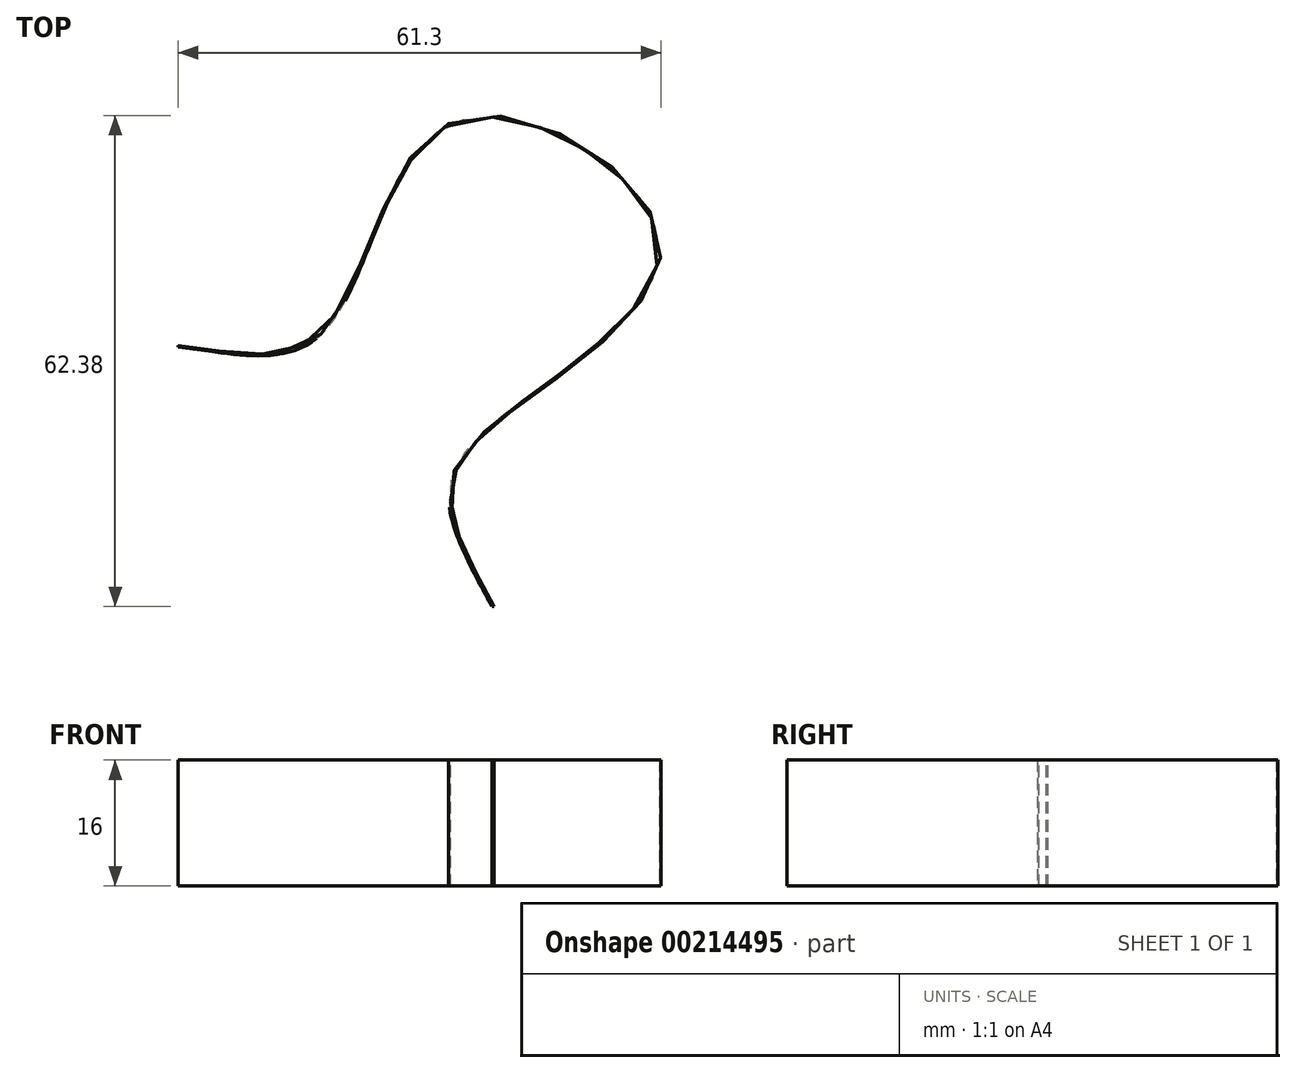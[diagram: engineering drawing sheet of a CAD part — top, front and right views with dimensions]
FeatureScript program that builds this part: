
annotation { "Feature Type Name" : "Feature", "Feature Type Description" : "" }
export const myFeature = defineFeature(function(context is Context, id is Id, definition is map)
    precondition{}
    {
        {
            var Q0;
            Q0=qCreatedBy(makeId("Top.planeOp"),FACE);
            var sketch = newSketch(context, id + "F0", { "sketchPlane" : qUnion([Q0])});
            skLineSegment(sketch, "E0.bottom", {"start": v(-49.02, 68.55) * mm, "end": v(50.98, 68.55) * mm});
            skLineSegment(sketch, "E0.top", {"start": v(-49.02, -1.45) * mm, "end": v(50.98, -1.45) * mm});
            skLineSegment(sketch, "E0.left", {"start": v(-49.02, 68.55) * mm, "end": v(-49.02, -1.45) * mm});
            skLineSegment(sketch, "E0.right", {"start": v(50.98, 68.55) * mm, "end": v(50.98, -1.45) * mm});
            skSolve(sketch);
        }
        {
            var Q0;
            Q0=makeQuery(id+"F0.imprint","IMPRINT",FACE,{"disambiguationData":[TD([[makeQuery(id+"F0.imprint","IMPRINT",EDGE,{"derivedFrom":sQuery(id+"F0.wireOp",EDGE,"E0.bottom")}),-1.0]])]});
            extrude(context, id + "F1", {"entities" : qUnion([Q0]), "depth" : 16 * mm});
        }
        {
            var Q0;
            Q0=makeQuery(id+"F1.opExtrude","CAP_FACE",FACE,{"disambiguationData":[OSD([sQuery(id+"F0.wireOp",EDGE,"E0.bottom"),sQuery(id+"F0.wireOp",EDGE,"E0.top"),sQuery(id+"F0.wireOp",EDGE,"E0.left"),sQuery(id+"F0.wireOp",EDGE,"E0.right")])],"isStart":false});
            var sketch = newSketch(context, id + "F2", { "sketchPlane" : qUnion([Q0])});
            skFitSpline(sketch, "E1", {"points": [v(-49.02, 32.72) * mm, v(-31.2, 34.1) * mm, v(-14.12, 61.19) * mm, v(12.2, 46.15) * mm, v(-7.24, 23.93) * mm, v(-14.44, 12.73) * mm, v(-8.38, -1.45) * mm], "startDerivative": vector(112.66, -9.86) * mm, "endDerivative": vector(43.43, -83.27) * mm});
            skSolve(sketch);
        }
        {
            var Q0;
            {var subQ5=makeQuery(id+"F1.opExtrude","CAP_EDGE",EDGE,{"disambiguationData":[OSD([sQuery(id+"F0.wireOp",EDGE,"E0.right")])],"isStart":false});Q0=makeQuery(id+"F2.imprint","IMPRINT",FACE,{"disambiguationData":[TD([[makeQuery(id+"F2.imprint","IMPRINT",EDGE,{"derivedFrom":subQ5}),-1.0]])]});}
            var Q1;
            {var subQ0=sQuery(id+"F2.wireOp",EDGE,"f820d5b4-2767-42e3-97d1-27e4c2d8213b");var subQ1=makeQuery(id+"F1.opExtrude","CAP_EDGE",EDGE,{"disambiguationData":[OSD([sQuery(id+"F0.wireOp",EDGE,"E0.left")])],"isStart":false});var subQ2=makeQuery(id+"F2.imprint","INTERSECT",VERTEX,{"derivedFrom":[subQ1,subQ0]});Q1=makeQuery(id+"F2.imprint","IMPRINT",FACE,{"disambiguationData":[TD([[makeQuery(id+"F2.imprint","IMPRINT",EDGE,{"disambiguationData":[TD([[subQ2,-1.0]])],"derivedFrom":subQ0}),1.0]])]});}
            extrude(context, id + "F3", {"entities" : qUnion([Q0, Q1]), "operationType" : NewBodyOperationType.REMOVE, "oppositeDirection" : true, "depth" : 25 * mm});
        }
        {
            var Q0;
            Q0=makeQuery(id+"F1.opExtrude","CAP_FACE",FACE,{"disambiguationData":[OSD([sQuery(id+"F0.wireOp",EDGE,"E0.bottom"),sQuery(id+"F0.wireOp",EDGE,"E0.top"),sQuery(id+"F0.wireOp",EDGE,"E0.left"),sQuery(id+"F0.wireOp",EDGE,"E0.right")])],"isStart":false});
            var Q1;
            Q1=makeQuery(id+"F1.opExtrude","CAP_FACE",FACE,{"disambiguationData":[OSD([sQuery(id+"F0.wireOp",EDGE,"E0.bottom"),sQuery(id+"F0.wireOp",EDGE,"E0.top"),sQuery(id+"F0.wireOp",EDGE,"E0.left"),sQuery(id+"F0.wireOp",EDGE,"E0.right")])],"isStart":true});
            var Q2;
            Q2=makeQuery(id+"F1.opExtrude","SWEPT_FACE",FACE,{"disambiguationData":[OSD([sQuery(id+"F0.wireOp",EDGE,"E0.left")])]});
            shell(context, id + "F4", {"entities" : qUnion([Q0, Q1, Q2]), "thickness" : 0.2 * mm});
        }
        {
            var Q0;
            Q0=makeQuery(id+"F1.opExtrude","SWEPT_FACE",FACE,{"disambiguationData":[OSD([sQuery(id+"F0.wireOp",EDGE,"E0.top")])]});
            extrude(context, id + "F5", {"entities" : qUnion([Q0]), "operationType" : NewBodyOperationType.REMOVE, "oppositeDirection" : true, "depth" : 1 * mm});
        }
    });
